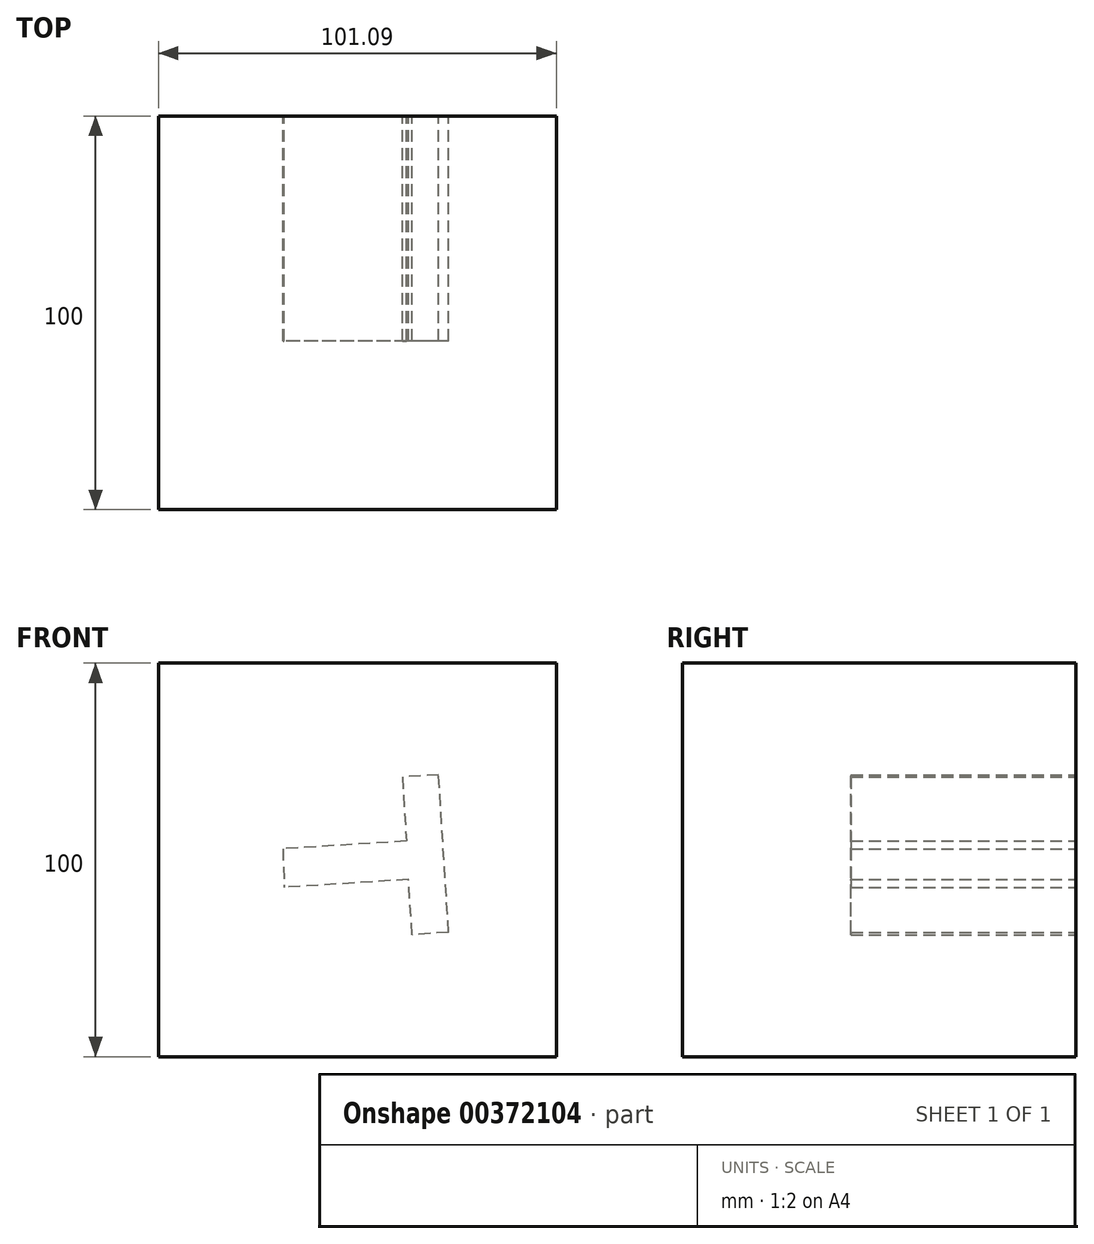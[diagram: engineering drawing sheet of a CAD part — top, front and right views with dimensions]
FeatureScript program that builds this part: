
annotation { "Feature Type Name" : "Feature", "Feature Type Description" : "" }
export const myFeature = defineFeature(function(context is Context, id is Id, definition is map)
    precondition{}
    {
        {
            var Q0;
            Q0=qCreatedBy(makeId("Right.planeOp"),FACE);
            var sketch = newSketch(context, id + "F0", { "sketchPlane" : qUnion([Q0])});
            skLineSegment(sketch, "E0", {"start": v(131.66, -54.78) * mm, "end": v(31.66, -54.78) * mm});
            skLineSegment(sketch, "E1", {"start": v(31.66, -54.78) * mm, "end": v(31.66, 45.22) * mm});
            skLineSegment(sketch, "E2", {"start": v(31.66, 45.22) * mm, "end": v(131.66, 45.22) * mm});
            skLineSegment(sketch, "E3", {"start": v(131.66, 45.22) * mm, "end": v(131.66, -54.78) * mm});
            skSolve(sketch);
        }
        {
            var Q0;
            Q0=makeQuery(id+"F0.imprint","IMPRINT",FACE,{"disambiguationData":[TD([[makeQuery(id+"F0.imprint","IMPRINT",EDGE,{"derivedFrom":sQuery(id+"F0.wireOp",EDGE,"E0")}),-1.0]])]});
            extrude(context, id + "F1", {"entities" : qUnion([Q0]), "depth" : 101.1 * mm});
        }
        {
            var Q0;
            Q0=makeQuery(id+"F1.opExtrude","SWEPT_FACE",FACE,{"disambiguationData":[OSD([sQuery(id+"F0.wireOp",EDGE,"E3")])]});
            var sketch = newSketch(context, id + "F2", { "sketchPlane" : qUnion([Q0])});
            skLineSegment(sketch, "E4", {"start": v(-73.7, -23.2) * mm, "end": v(-71.18, 16.84) * mm});
            skLineSegment(sketch, "E5", {"start": v(-73.7, -23.2) * mm, "end": v(-64.42, -23.78) * mm});
            skLineSegment(sketch, "E6", {"start": v(-71.18, 16.84) * mm, "end": v(-61.95, 16.25) * mm});
            skLineSegment(sketch, "E7", {"start": v(-61.95, 16.25) * mm, "end": v(-62.97, 0) * mm});
            skLineSegment(sketch, "E8", {"start": v(-64.42, -23.78) * mm, "end": v(-63.54, -9.77) * mm});
            skLineSegment(sketch, "E9", {"start": v(-63.54, -9.77) * mm, "end": v(-31.94, -11.76) * mm});
            skLineSegment(sketch, "E10", {"start": v(-62.97, 0) * mm, "end": v(-31.63, -1.97) * mm});
            skLineSegment(sketch, "E11", {"start": v(-31.63, -1.97) * mm, "end": v(-31.94, -11.76) * mm});
            skSolve(sketch);
        }
        {
            var Q0;
            Q0 = qSketchRegion(id + "F2", true);
            extrude(context, id + "F3", {"entities" : qUnion([Q0]), "operationType" : NewBodyOperationType.REMOVE, "oppositeDirection" : true, "depth" : 57.15 * mm});
        }
    });
